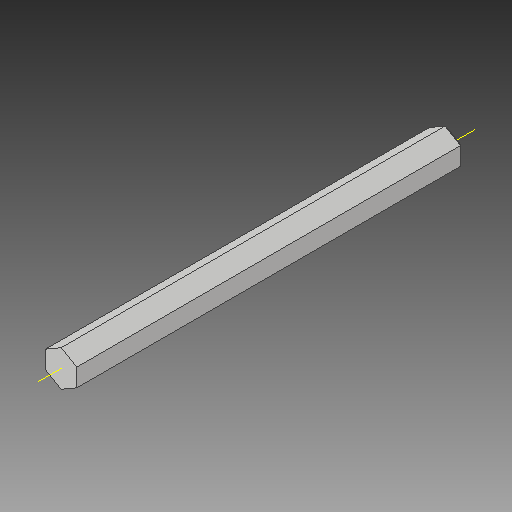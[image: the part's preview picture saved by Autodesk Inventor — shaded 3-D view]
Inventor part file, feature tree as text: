
AUTODESK INVENTOR PART (.ipt)
format: ipt  version: 2019 (Build 230136000, 136)  size: 107,520 bytes
history: native  units: in
note: dims shown in document units (in); Inventor stores cm internally (conversion verified against a paired STEP export)
features: sketch x2, extrude x1, other x1
ambient origin geometry x8: Origin, YZ Plane, XZ Plane, XY Plane, X Axis, Y Axis, Z Axis, Center Point
bodies: Solid2 (feature_tree), Solid1 (feature_tree)
feature tree (4):
  extrude  "Extrusion1"  [1 undecoded]
  sketch  "Sketch2"
  other  "Work Axis1"
  sketch  "Sketch1"  dims[d0=2.875in d1=0.0in]
note: 1 required parameter value undecoded (feature->parameter linkage not recoverable at this tier; creation-order binding heuristic only, values carry confidence <= 0.55)
